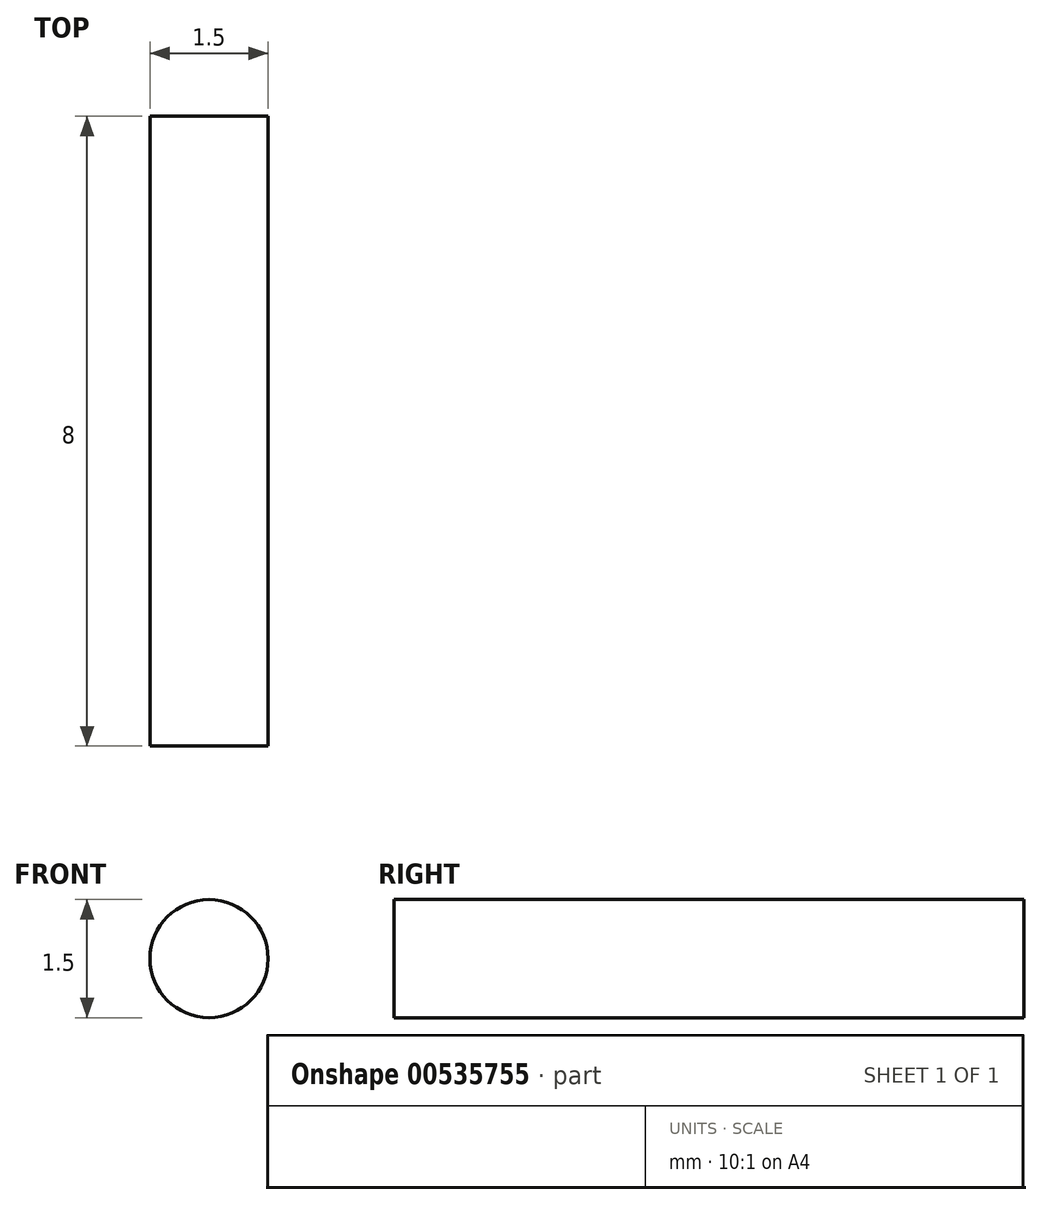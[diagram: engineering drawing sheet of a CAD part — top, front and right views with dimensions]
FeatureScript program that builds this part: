
annotation { "Feature Type Name" : "Feature", "Feature Type Description" : "" }
export const myFeature = defineFeature(function(context is Context, id is Id, definition is map)
    precondition{}
    {
        {
            var Q0;
            Q0=qCreatedBy(makeId("Front.planeOp"),FACE);
            var sketch = newSketch(context, id + "F0", { "sketchPlane" : qUnion([Q0])});
            skCircle(sketch, "E0", {"center": v(0, 0) * mm, "radius": 0.75 * mm});
            skSolve(sketch);
        }
        {
            var Q0;
            Q0 = qSketchRegion(id + "F0", true);
            extrude(context, id + "F1", {"entities" : qUnion([Q0]), "depth" : 8 * mm, "offsetDistance" : 25 * mm});
        }
    });
